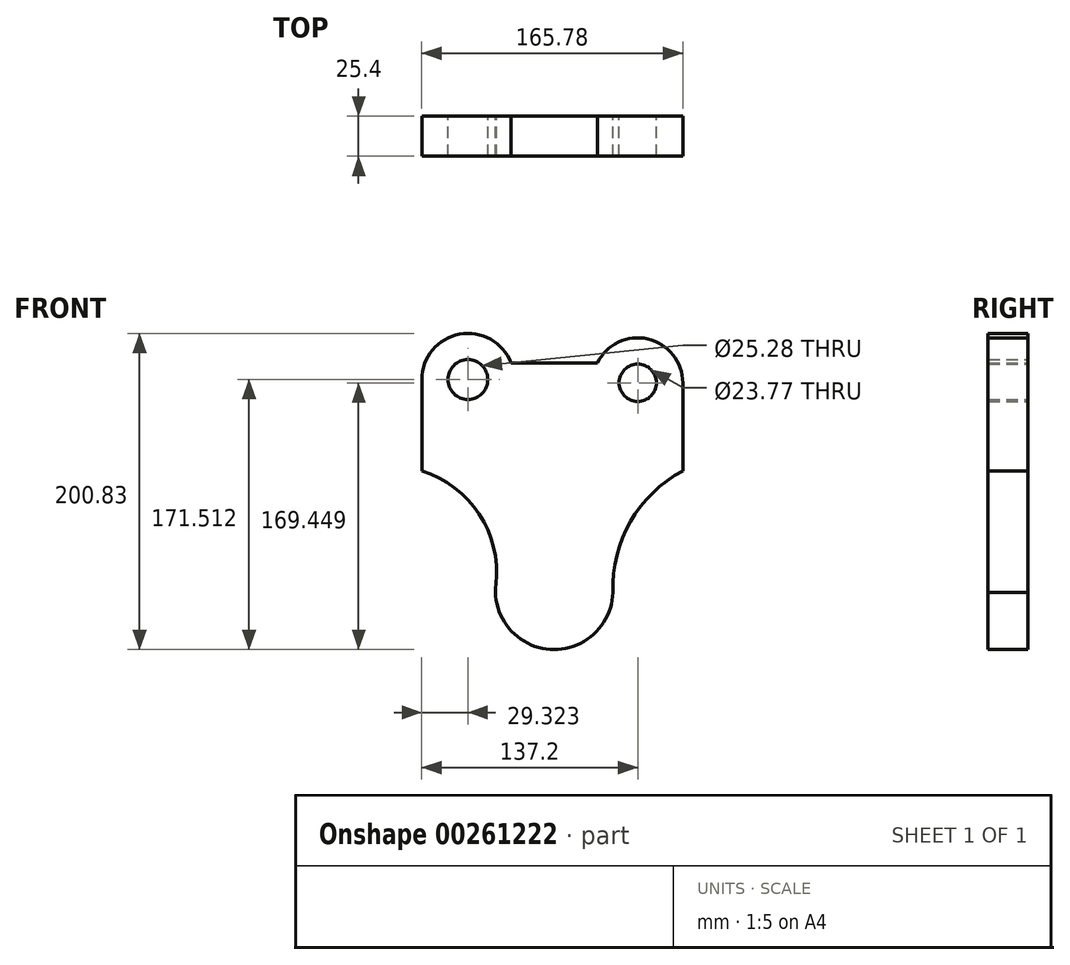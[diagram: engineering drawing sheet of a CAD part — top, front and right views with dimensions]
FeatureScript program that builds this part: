
annotation { "Feature Type Name" : "Feature", "Feature Type Description" : "" }
export const myFeature = defineFeature(function(context is Context, id is Id, definition is map)
    precondition{}
    {
        {
            var Q0;
            Q0=qCreatedBy(makeId("Front.planeOp"),FACE);
            var sketch = newSketch(context, id + "F0", { "sketchPlane" : qUnion([Q0])});
            skArc(sketch, "E0", {"start": v(-27.4, 68.58) * mm, "mid": v(-60.1, 86.91) * mm, "end": v(-84.09, 58.08) * mm});
            skArc(sketch, "E1", {"start": v(81.68, 56.02) * mm, "mid": v(59.55, 83.85) * mm, "end": v(27.45, 68.58) * mm});
            skCircle(sketch, "E2", {"center": v(53.11, 56.02) * mm, "radius": 11.88 * mm});
            skCircle(sketch, "E3", {"center": v(-54.77, 58.08) * mm, "radius": 12.64 * mm});
            skArc(sketch, "E4", {"start": v(-37.05, -71.9) * mm, "mid": v(-1, -113.42) * mm, "end": v(37.23, -73.9) * mm});
            skLineSegment(sketch, "E5", {"start": v(-27.4, 68.58) * mm, "end": v(27.45, 68.58) * mm});
            skLineSegment(sketch, "E6", {"start": v(81.68, 56.02) * mm, "end": v(81.69, 0) * mm});
            skLineSegment(sketch, "E7", {"start": v(-84.09, 58.08) * mm, "end": v(-84.09, 0) * mm});
            skArc(sketch, "E8", {"start": v(81.69, 0) * mm, "mid": v(48.43, -32.23) * mm, "end": v(37.28, -77.17) * mm});
            skArc(sketch, "E9", {"start": v(-37.05, -71.9) * mm, "mid": v(-47.59, -27.46) * mm, "end": v(-84.09, 0) * mm});
            skSolve(sketch);
        }
        {
            var Q0;
            Q0=makeQuery(id+"F0.imprint","IMPRINT",FACE,{"disambiguationData":[TD([[makeQuery(id+"F0.imprint","IMPRINT",EDGE,{"derivedFrom":sQuery(id+"F0.wireOp",EDGE,"E0")}),1.0]])]});
            extrude(context, id + "F1", {"entities" : qUnion([Q0]), "depth" : 25.4 * mm});
        }
    });
